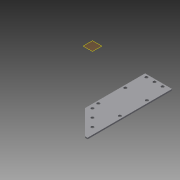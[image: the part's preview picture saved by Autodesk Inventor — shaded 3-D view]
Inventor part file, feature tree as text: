
AUTODESK INVENTOR PART (.ipt)
format: ipt  version: 2013 (Build 170138000, 138)  size: 109,568 bytes
history: native  units: in
note: dims shown in document units (in); Inventor stores cm internally (conversion verified against a paired STEP export)
features: sketch x1, plane x1, extrude x1
ambient origin geometry x8: Origin, YZ Plane, XZ Plane, XY Plane, X Axis, Y Axis, Z Axis, Center Point
bodies: Solid1 (feature_tree)
feature tree (3):
  sketch  "Sketch1"  dims[d34=12.0in d36=16.0in d38=45.0deg d40=0.266in d41=0.266in d42=0.266in d43=0.266in d44=0.25in d45=0.25in d46=0.25in d48=0.25in d49=0.25in d50=0.25in d51=0.25in d52=0.25in d53=157.5deg d58=0.266in d59=0.266in d64=0.266in d70=0.266in d72=2.5in d73=0.125in d74=0.0in]
  plane  "Work Plane1"
  extrude  "Extrusion5"  Depth=16.0in
